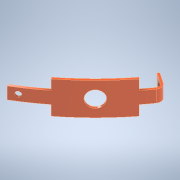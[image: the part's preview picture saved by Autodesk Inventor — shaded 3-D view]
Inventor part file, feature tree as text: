
AUTODESK INVENTOR PART (.ipt)
format: ipt  version: 2021 (Build 250183000, 183)  size: 204,288 bytes
history: native  units: in
note: dims shown in document units (in); Inventor stores cm internally (conversion verified against a paired STEP export)
features: other x5, sketch x4, extrude x1, plane x1
ambient origin geometry x8: Origin, YZ Plane, XZ Plane, XY Plane, X Axis, Y Axis, Z Axis, Center Point
bodies: Solid1 (feature_tree)
feature tree (11):
  extrude  "Extrusion1"  Depth=1.151in
  other  "Bend Part1"
  other  "Bend Part2"
  other  "Work Axis1"
  other  "Work Axis2"
  plane  "Work Plane1"
  sketch  "Sketch4"  dims[d6=0.0926in d8=0.11in d9=0.11in d10=0.0924in d11=0.218in d12=0.051in d13=0.055in d14=0.055in d15=0.051in d16=0.218in d17=0.1475in d18=0.148in d19=0.5755in d20=0.02in d21=0.0in d22=0.0394in d23=90.0deg d24=0.571in d25=0.2855in d26=2.36in d27=360.0deg d28=0.148in d29=0.15in]
  other  "Work Axis3"
  sketch  "Sketch1"  dims[d2=0.295in d3=1.151in]
  sketch  "Sketch2"  dims[d4=0.29in]
  sketch  "Sketch3"  dims[d5=0.29in]
